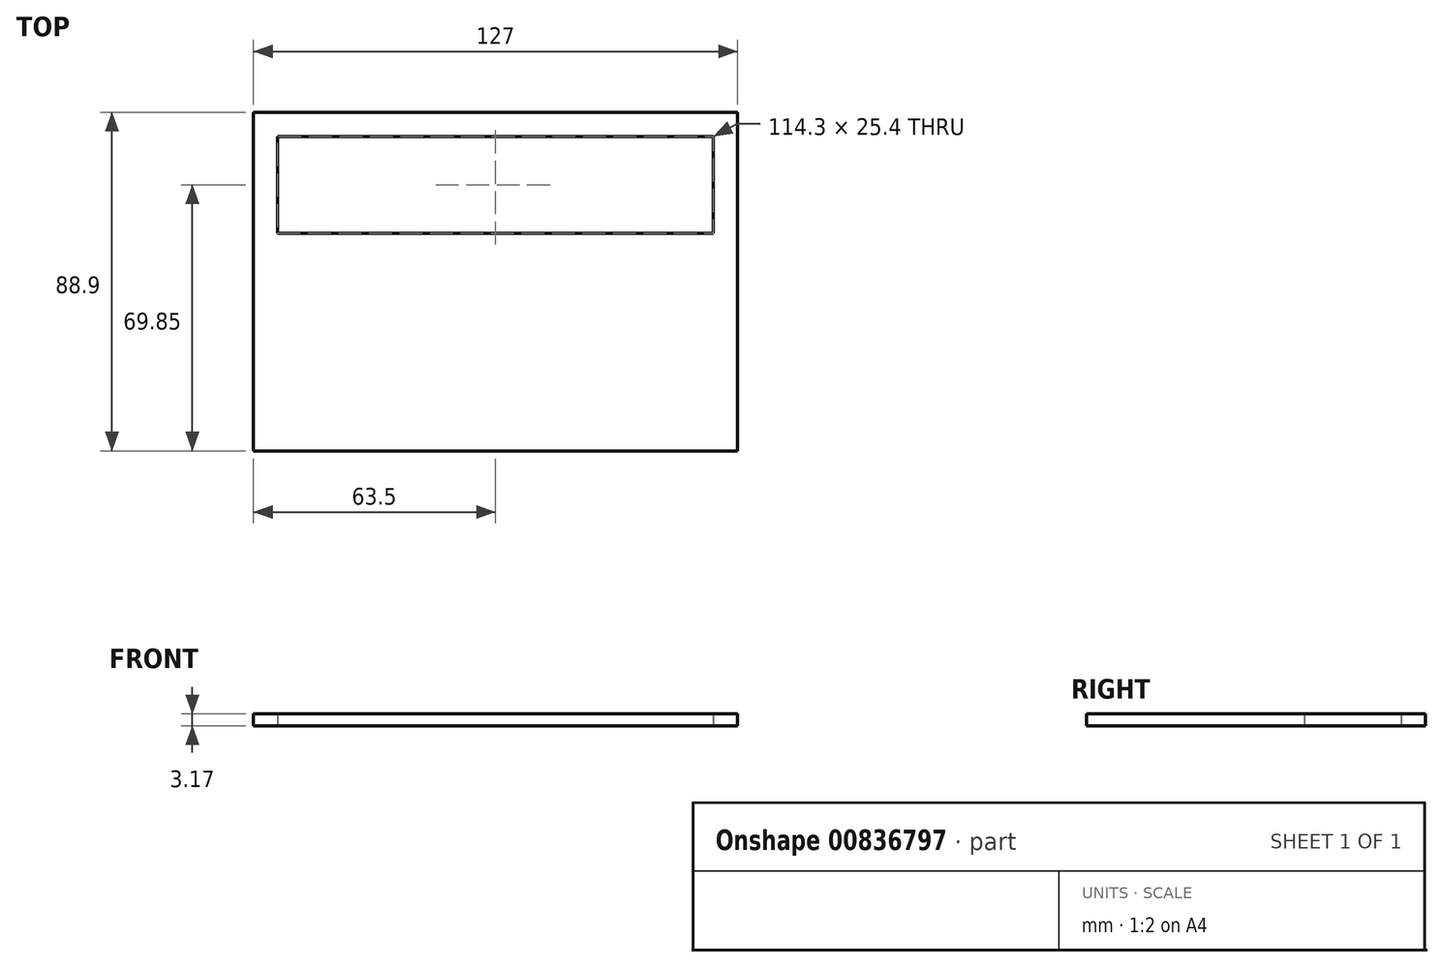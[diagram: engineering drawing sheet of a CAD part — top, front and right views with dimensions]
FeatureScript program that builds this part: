
annotation { "Feature Type Name" : "Feature", "Feature Type Description" : "" }
export const myFeature = defineFeature(function(context is Context, id is Id, definition is map)
    precondition{}
    {
        {
            var Q0;
            Q0=qCreatedBy(makeId("Top.planeOp"),FACE);
            var sketch = newSketch(context, id + "F0", { "sketchPlane" : qUnion([Q0])});
            skLineSegment(sketch, "E0.bottom", {"start": v(-63.5, 63.5) * mm, "end": v(63.5, 63.5) * mm});
            skLineSegment(sketch, "E0.top", {"start": v(-63.5, -25.4) * mm, "end": v(63.5, -25.4) * mm});
            skLineSegment(sketch, "E0.left", {"start": v(-63.5, 63.5) * mm, "end": v(-63.5, -25.4) * mm});
            skLineSegment(sketch, "E0.right", {"start": v(63.5, 63.5) * mm, "end": v(63.5, -25.4) * mm});
            skLineSegment(sketch, "E1.bottom", {"start": v(-57.15, 57.15) * mm, "end": v(57.15, 57.15) * mm});
            skLineSegment(sketch, "E1.top", {"start": v(-57.15, 31.75) * mm, "end": v(57.15, 31.75) * mm});
            skLineSegment(sketch, "E1.left", {"start": v(-57.15, 57.15) * mm, "end": v(-57.15, 31.75) * mm});
            skLineSegment(sketch, "E1.right", {"start": v(57.15, 57.15) * mm, "end": v(57.15, 31.75) * mm});
            skSolve(sketch);
        }
        {
            var Q0;
            Q0 = qSketchRegion(id + "F0", true);
            extrude(context, id + "F1", {"entities" : qUnion([Q0]), "depth" : 3.17 * mm, "offsetDistance" : 25.4 * mm});
        }
    });
